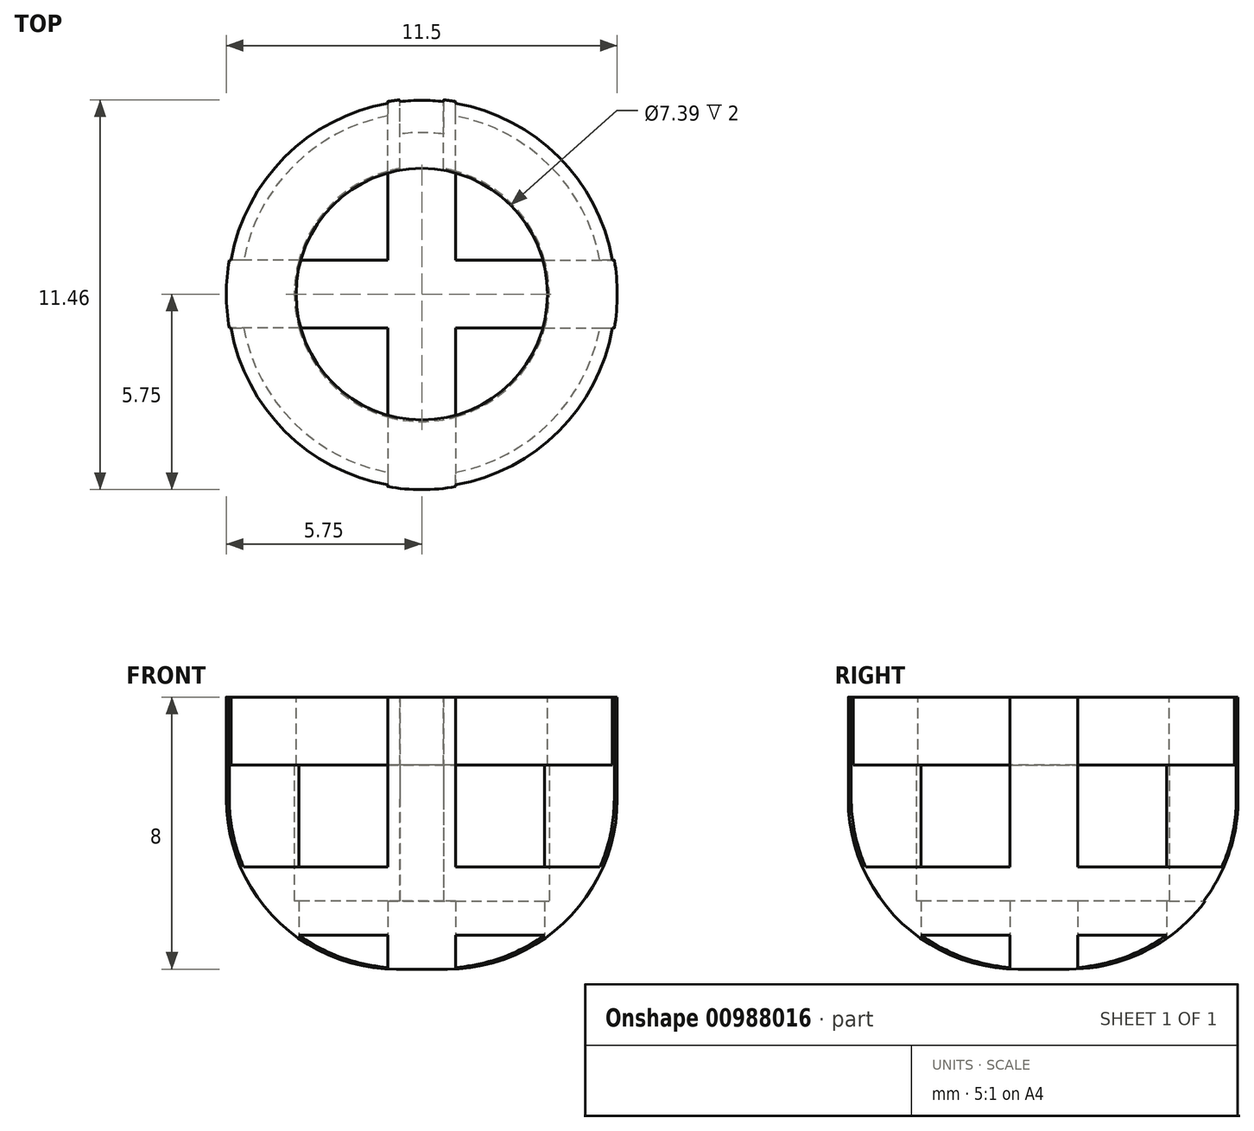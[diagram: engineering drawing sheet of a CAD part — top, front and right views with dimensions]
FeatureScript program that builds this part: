
annotation { "Feature Type Name" : "Feature", "Feature Type Description" : "" }
export const myFeature = defineFeature(function(context is Context, id is Id, definition is map)
    precondition{}
    {
        {
            var Q0;
            Q0=qCreatedBy(makeId("Top.planeOp"),FACE);
            var sketch = newSketch(context, id + "F0", { "sketchPlane" : qUnion([Q0])});
            skCircle(sketch, "E0", {"center": v(0, 0) * mm, "radius": 3.75 * mm});
            skCircle(sketch, "E1", {"center": v(0, 0) * mm, "radius": 5.75 * mm});
            skPoint(sketch, "E2.middle", {"position": v(0, 3.75) * mm});
            skLineSegment(sketch, "E3.bottom", {"start": v(0.65, 3.17) * mm, "end": v(-0.65, 3.17) * mm});
            skLineSegment(sketch, "E3.top", {"start": v(0.65, 6.42) * mm, "end": v(-0.65, 6.42) * mm});
            skLineSegment(sketch, "E3.left", {"start": v(0.65, 3.17) * mm, "end": v(0.65, 6.42) * mm});
            skLineSegment(sketch, "E3.right", {"start": v(-0.65, 3.17) * mm, "end": v(-0.65, 6.42) * mm});
            skPoint(sketch, "E3.middle", {"position": v(0, 4.8) * mm});
            skLineSegment(sketch, "E4", {"start": v(1, 3.61) * mm, "end": v(1, -3.61) * mm});
            skLineSegment(sketch, "E5", {"start": v(-1, 3.61) * mm, "end": v(-1, -3.61) * mm});
            skLineSegment(sketch, "E6", {"start": v(-3.61, -1) * mm, "end": v(3.77, -1) * mm});
            skLineSegment(sketch, "E7", {"start": v(3.61, 1) * mm, "end": v(-3.61, 1) * mm});
            skLineSegment(sketch, "E8", {"start": v(-1, 3.61) * mm, "end": v(-1, 5.66) * mm});
            skLineSegment(sketch, "E9", {"start": v(1, 3.61) * mm, "end": v(1, 5.66) * mm});
            skLineSegment(sketch, "E10.MirrorCS", {"start": v(1, -3.61) * mm, "end": v(1, -5.66) * mm});
            skLineSegment(sketch, "E11.MirrorCS", {"start": v(-1, -3.61) * mm, "end": v(-1, -5.66) * mm});
            skLineSegment(sketch, "E12", {"start": v(-3.61, 1) * mm, "end": v(-5.66, 1) * mm});
            skLineSegment(sketch, "E13", {"start": v(-3.61, -1) * mm, "end": v(-5.66, -1) * mm});
            skLineSegment(sketch, "E14.MirrorCS", {"start": v(3.61, 1) * mm, "end": v(5.66, 1) * mm});
            skLineSegment(sketch, "E15.MirrorCS", {"start": v(3.61, -1) * mm, "end": v(5.66, -1) * mm});
            skSolve(sketch);
        }
        {
            var Q0;
            {var subQ4=sQuery(id+"F0.wireOp",EDGE,"E10.MirrorCS");Q0=makeQuery(id+"F0.imprint","IMPRINT",FACE,{"disambiguationData":[TD([[makeQuery(id+"F0.imprint","IMPRINT",EDGE,{"derivedFrom":subQ4}),1.0]])]});}
            var Q1;
            {var subQ0=sQuery(id+"F0.wireOp",EDGE,"E11.MirrorCS");Q1=makeQuery(id+"F0.imprint","IMPRINT",FACE,{"disambiguationData":[TD([[makeQuery(id+"F0.imprint","IMPRINT",EDGE,{"derivedFrom":subQ0}),-1.0]])]});}
            var Q2;
            {var subQ0=sQuery(id+"F0.wireOp",EDGE,"E8");Q2=makeQuery(id+"F0.imprint","IMPRINT",FACE,{"disambiguationData":[TD([[makeQuery(id+"F0.imprint","IMPRINT",EDGE,{"derivedFrom":subQ0}),1.0]])]});}
            var Q3;
            {var subQ0=sQuery(id+"F0.wireOp",EDGE,"E9");Q3=makeQuery(id+"F0.imprint","IMPRINT",FACE,{"disambiguationData":[TD([[makeQuery(id+"F0.imprint","IMPRINT",EDGE,{"derivedFrom":subQ0}),-1.0]])]});}
            extrude(context, id + "F1", {"entities" : qUnion([Q0, Q1, Q2, Q3]), "depth" : 3 * mm, "offsetDistance" : 25 * mm});
        }
        {
            var Q0;
            {var subQ0=sQuery(id+"F0.wireOp",EDGE,"E9");Q0=makeQuery(id+"F0.imprint","IMPRINT",FACE,{"disambiguationData":[TD([[makeQuery(id+"F0.imprint","IMPRINT",EDGE,{"derivedFrom":subQ0}),1.0]])]});}
            var Q1;
            {var subQ0=sQuery(id+"F0.wireOp",EDGE,"E8");Q1=makeQuery(id+"F0.imprint","IMPRINT",FACE,{"disambiguationData":[TD([[makeQuery(id+"F0.imprint","IMPRINT",EDGE,{"derivedFrom":subQ0}),-1.0]])]});}
            var Q2;
            {var subQ2=sQuery(id+"F0.wireOp",EDGE,"E12");Q2=makeQuery(id+"F0.imprint","IMPRINT",FACE,{"disambiguationData":[TD([[makeQuery(id+"F0.imprint","IMPRINT",EDGE,{"derivedFrom":subQ2}),1.0]])]});}
            var Q3;
            {var subQ4=sQuery(id+"F0.wireOp",EDGE,"E14.MirrorCS");Q3=makeQuery(id+"F0.imprint","IMPRINT",FACE,{"disambiguationData":[TD([[makeQuery(id+"F0.imprint","IMPRINT",EDGE,{"derivedFrom":subQ4}),-1.0]])]});}
            var Q4;
            {var subQ0=sQuery(id+"F0.wireOp",EDGE,"E10.MirrorCS");Q4=makeQuery(id+"F0.imprint","IMPRINT",FACE,{"disambiguationData":[TD([[makeQuery(id+"F0.imprint","IMPRINT",EDGE,{"derivedFrom":subQ0}),-1.0]])]});}
            extrude(context, id + "F2", {"entities" : qUnion([Q0, Q1, Q2, Q3, Q4]), "operationType" : NewBodyOperationType.ADD, "surfaceOperationType" : NewSurfaceOperationType.ADD, "depth" : 8 * mm, "offsetDistance" : 25 * mm});
        }
        {
            var Q0;
            {var subQ0=sQuery(id+"F0.wireOp",EDGE,"E3.left");var subQ1=sQuery(id+"F0.wireOp",EDGE,"E0");var subQ2=makeQuery(id+"F0.imprint","INTERSECT",VERTEX,{"derivedFrom":[subQ1,subQ0]});Q0=makeQuery(id+"F0.imprint","IMPRINT",FACE,{"disambiguationData":[TD([[makeQuery(id+"F0.imprint","IMPRINT",EDGE,{"disambiguationData":[TD([[subQ2,-1.0]])],"derivedFrom":subQ1}),-1.0]])]});}
            var Q1;
            {var subQ5=sQuery(id+"F0.wireOp",EDGE,"E3.bottom");Q1=makeQuery(id+"F0.imprint","IMPRINT",FACE,{"disambiguationData":[TD([[makeQuery(id+"F0.imprint","IMPRINT",EDGE,{"derivedFrom":subQ5}),-1.0]])]});}
            var Q2;
            {var subQ1=sQuery(id+"F0.wireOp",EDGE,"E3.bottom");Q2=makeQuery(id+"F0.imprint","IMPRINT",FACE,{"disambiguationData":[TD([[makeQuery(id+"F0.imprint","IMPRINT",EDGE,{"derivedFrom":subQ1}),1.0]])]});}
            var Q3;
            {var subQ3=sQuery(id+"F0.wireOp",EDGE,"E7");var subQ5=sQuery(id+"F0.wireOp",EDGE,"E5");var subQ6=makeQuery(id+"F0.imprint","INTERSECT",VERTEX,{"derivedFrom":[subQ5,subQ3]});Q3=makeQuery(id+"F0.imprint","IMPRINT",FACE,{"disambiguationData":[TD([[makeQuery(id+"F0.imprint","IMPRINT",EDGE,{"disambiguationData":[TD([[subQ6,-1.0]])],"derivedFrom":subQ5}),-1.0]])]});}
            var Q4;
            {var subQ3=sQuery(id+"F0.wireOp",EDGE,"E7");var subQ5=sQuery(id+"F0.wireOp",EDGE,"E4");var subQ6=makeQuery(id+"F0.imprint","INTERSECT",VERTEX,{"derivedFrom":[subQ5,subQ3]});Q4=makeQuery(id+"F0.imprint","IMPRINT",FACE,{"disambiguationData":[TD([[makeQuery(id+"F0.imprint","IMPRINT",EDGE,{"disambiguationData":[TD([[subQ6,-1.0]])],"derivedFrom":subQ5}),1.0]])]});}
            var Q5;
            {var subQ0=sQuery(id+"F0.wireOp",EDGE,"E7");var subQ1=sQuery(id+"F0.wireOp",EDGE,"E4");var subQ2=makeQuery(id+"F0.imprint","INTERSECT",VERTEX,{"derivedFrom":[subQ1,subQ0]});Q5=makeQuery(id+"F0.imprint","IMPRINT",FACE,{"disambiguationData":[TD([[makeQuery(id+"F0.imprint","IMPRINT",EDGE,{"disambiguationData":[TD([[subQ2,-1.0]])],"derivedFrom":subQ1}),-1.0]])]});}
            var Q6;
            {var subQ0=sQuery(id+"F0.wireOp",EDGE,"E4");var subQ5=sQuery(id+"F0.wireOp",EDGE,"E6");var subQ6=makeQuery(id+"F0.imprint","INTERSECT",VERTEX,{"derivedFrom":[subQ0,subQ5]});Q6=makeQuery(id+"F0.imprint","IMPRINT",FACE,{"disambiguationData":[TD([[makeQuery(id+"F0.imprint","IMPRINT",EDGE,{"disambiguationData":[TD([[subQ6,1.0]])],"derivedFrom":subQ5}),-1.0]])]});}
            extrude(context, id + "F3", {"entities" : qUnion([Q0, Q1, Q2, Q3, Q4, Q5, Q6]), "operationType" : NewBodyOperationType.ADD, "depth" : 2 * mm, "offsetDistance" : 25 * mm});
        }
        {
            var Q0;
            Q0=makeQuery(id+"F2.opExtrude","CAP_FACE",FACE,{"disambiguationData":[OSD([sQuery(id+"F0.wireOp",EDGE,"E0"),sQuery(id+"F0.wireOp",EDGE,"E1"),sQuery(id+"F0.wireOp",EDGE,"E14.MirrorCS"),sQuery(id+"F0.wireOp",EDGE,"E15.MirrorCS")])],"isStart":false});
            var sketch = newSketch(context, id + "F4", { "sketchPlane" : qUnion([Q0])});
            skCircle(sketch, "E16", {"center": v(0, 0) * mm, "radius": 3.7 * mm});
            skCircle(sketch, "E17", {"center": v(0, 0) * mm, "radius": 5.7 * mm});
            skSolve(sketch);
        }
        {
            var Q0;
            Q0=makeQuery(id+"F4.imprint","IMPRINT",FACE,{"disambiguationData":[TD([[makeQuery(id+"F4.imprint","IMPRINT",EDGE,{"derivedFrom":sQuery(id+"F4.wireOp",EDGE,"E16")}),-1.0]])]});
            extrude(context, id + "F5", {"entities" : qUnion([Q0]), "operationType" : NewBodyOperationType.ADD, "oppositeDirection" : true, "depth" : 2 * mm, "offsetDistance" : 25 * mm});
        }
        {
            var Q0;
            {var subQ0=sQuery(id+"F0.wireOp",EDGE,"E1");var subQ1=makeQuery(id+"F0.imprint","INTERSECT",VERTEX,{"derivedFrom":[subQ0,sQuery(id+"F0.wireOp",EDGE,"E14.MirrorCS")]});var subQ3=makeQuery(id+"F0.imprint","INTERSECT",VERTEX,{"derivedFrom":[subQ0,sQuery(id+"F0.wireOp",EDGE,"E10.MirrorCS")]});var subQ4=makeQuery(id+"F0.imprint","INTERSECT",VERTEX,{"derivedFrom":[subQ0,sQuery(id+"F0.wireOp",EDGE,"E11.MirrorCS")]});var subQ5=makeQuery(id+"F0.imprint","INTERSECT",VERTEX,{"derivedFrom":[subQ0,sQuery(id+"F0.wireOp",EDGE,"E12")]});var subQ7=makeQuery(id+"F0.imprint","INTERSECT",VERTEX,{"derivedFrom":[subQ0,sQuery(id+"F0.wireOp",EDGE,"E8")]});var subQ8=makeQuery(id+"F0.imprint","INTERSECT",VERTEX,{"derivedFrom":[subQ0,sQuery(id+"F0.wireOp",EDGE,"E9")]});Q0=makeQuery(id+"F3.boolean.opBoolean","MERGE",EDGE,{"derivedFrom":[makeQuery(id+"F2.boolean.opBoolean","MERGE",EDGE,{"derivedFrom":[makeQuery(id+"F1.opExtrude","CAP_EDGE",EDGE,{"disambiguationData":[OSD([subQ0]),TDD([makeQuery(id+"F0.imprint","IMPRINT",EDGE,{"disambiguationData":[TD([[subQ8,1.0]])],"derivedFrom":subQ0})])],"isStart":true}),makeQuery(id+"F1.opExtrude","CAP_EDGE",EDGE,{"disambiguationData":[OSD([subQ0]),TDD([makeQuery(id+"F0.imprint","IMPRINT",EDGE,{"disambiguationData":[TD([[subQ7,-1.0]])],"derivedFrom":subQ0})])],"isStart":true}),makeQuery(id+"F1.opExtrude","CAP_EDGE",EDGE,{"disambiguationData":[OSD([subQ0]),TDD([makeQuery(id+"F0.imprint","IMPRINT",EDGE,{"disambiguationData":[TD([[subQ4,1.0]])],"derivedFrom":subQ0})])],"isStart":true}),makeQuery(id+"F1.opExtrude","CAP_EDGE",EDGE,{"disambiguationData":[OSD([subQ0]),TDD([makeQuery(id+"F0.imprint","IMPRINT",EDGE,{"disambiguationData":[TD([[subQ3,-1.0]])],"derivedFrom":subQ0})])],"isStart":true}),makeQuery(id+"F2.opExtrude","CAP_EDGE",EDGE,{"disambiguationData":[OSD([subQ0]),TDD([makeQuery(id+"F0.imprint","IMPRINT",EDGE,{"disambiguationData":[TD([[subQ8,-1.0]])],"derivedFrom":subQ0})])],"isStart":true}),makeQuery(id+"F2.opExtrude","CAP_EDGE",EDGE,{"disambiguationData":[OSD([subQ0]),TDD([makeQuery(id+"F0.imprint","IMPRINT",EDGE,{"disambiguationData":[TD([[subQ7,1.0]])],"derivedFrom":subQ0})])],"isStart":true}),makeQuery(id+"F2.opExtrude","CAP_EDGE",EDGE,{"disambiguationData":[OSD([subQ0]),TDD([makeQuery(id+"F0.imprint","IMPRINT",EDGE,{"disambiguationData":[TD([[subQ5,-1.0]])],"derivedFrom":subQ0})])],"isStart":true}),makeQuery(id+"F2.opExtrude","CAP_EDGE",EDGE,{"disambiguationData":[OSD([subQ0]),TDD([makeQuery(id+"F0.imprint","IMPRINT",EDGE,{"disambiguationData":[TD([[subQ3,1.0]])],"derivedFrom":subQ0})])],"isStart":true}),makeQuery(id+"F2.opExtrude","CAP_EDGE",EDGE,{"disambiguationData":[OSD([subQ0]),TDD([makeQuery(id+"F0.imprint","IMPRINT",EDGE,{"disambiguationData":[TD([[subQ1,1.0]])],"derivedFrom":subQ0})])],"isStart":true})]}),makeQuery(id+"F3.opExtrude","CAP_EDGE",EDGE,{"disambiguationData":[OSD([subQ0])],"isStart":true})]});}
            fillet(context, id + "F6", {"entities" : qUnion([Q0]), "radius" : 5 * mm, "tangentPropagation" : true, "allowEdgeOverflow" : false});
        }
    });
